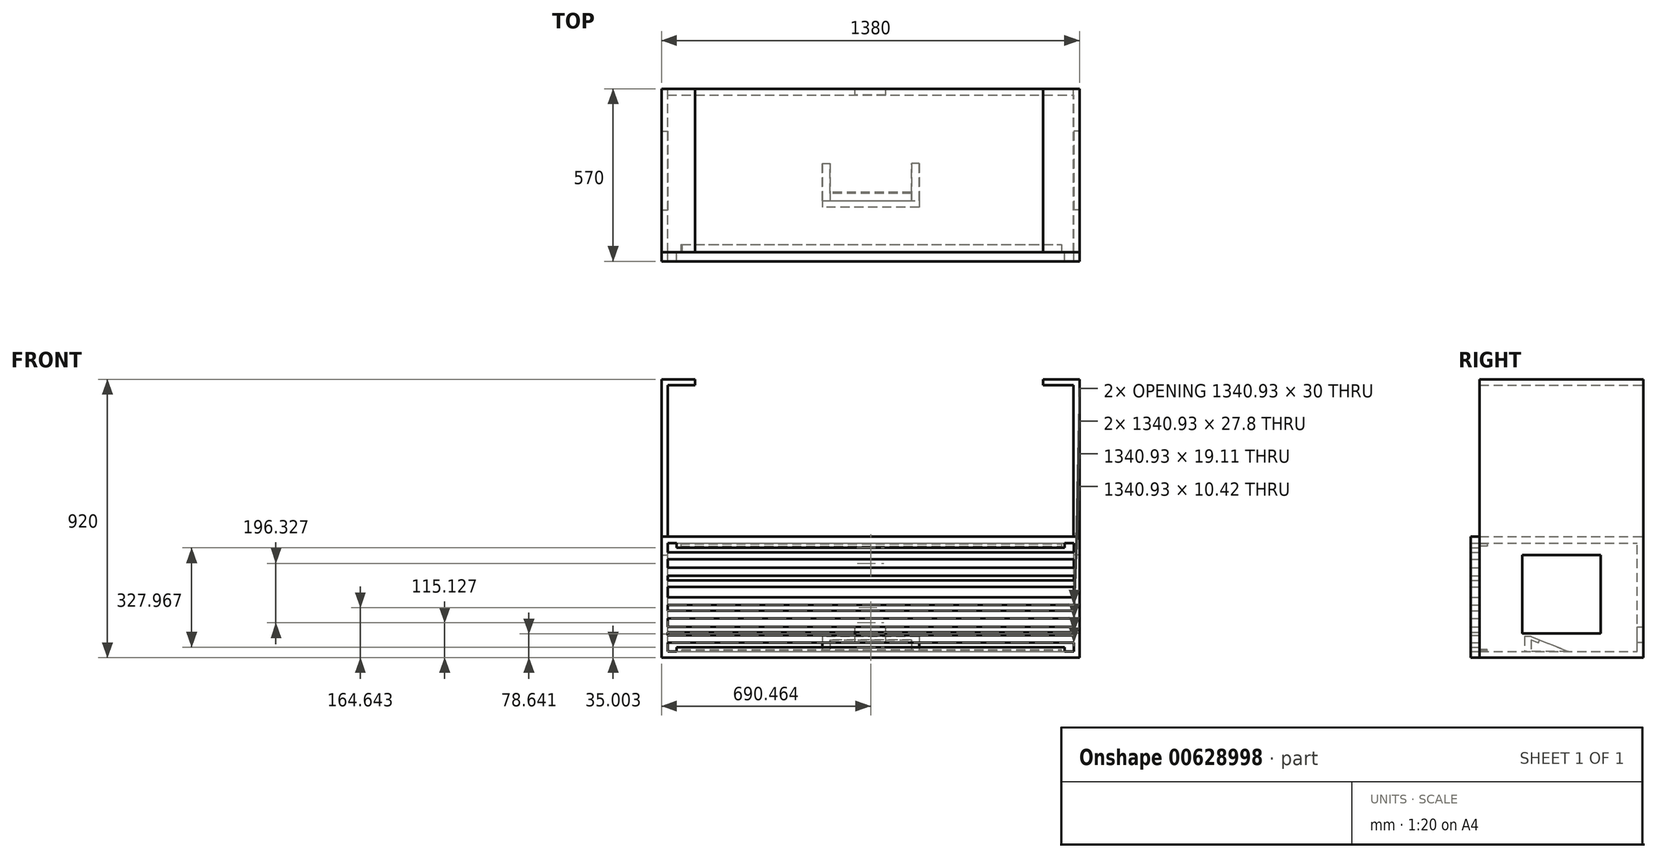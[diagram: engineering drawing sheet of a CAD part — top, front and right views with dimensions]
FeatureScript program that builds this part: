
annotation { "Feature Type Name" : "Feature", "Feature Type Description" : "" }
export const myFeature = defineFeature(function(context is Context, id is Id, definition is map)
    precondition{}
    {
        {
            var Q0;
            Q0=qCreatedBy(makeId("Front.planeOp"),FACE);
            var sketch = newSketch(context, id + "F0", { "sketchPlane" : qUnion([Q0])});
            skLineSegment(sketch, "E0", {"start": v(-401.13, 629.38) * mm, "end": v(-401.13, 129.38) * mm});
            skLineSegment(sketch, "E1", {"start": v(-401.13, -250.62) * mm, "end": v(938.87, -250.62) * mm});
            skLineSegment(sketch, "E2", {"start": v(-401.13, 629.38) * mm, "end": v(-361.13, 629.38) * mm});
            skLineSegment(sketch, "E3", {"start": v(938.87, 629.38) * mm, "end": v(838.87, 629.38) * mm});
            skLineSegment(sketch, "E4", {"start": v(-361.13, 629.38) * mm, "end": v(-361.13, 649.38) * mm});
            skLineSegment(sketch, "E5", {"start": v(-361.13, 649.38) * mm, "end": v(-421.13, 649.38) * mm});
            skLineSegment(sketch, "E6", {"start": v(-421.13, 649.38) * mm, "end": v(-421.13, -270.62) * mm});
            skLineSegment(sketch, "E7", {"start": v(-421.13, -270.62) * mm, "end": v(958.87, -270.62) * mm});
            skLineSegment(sketch, "E8", {"start": v(958.87, -270.62) * mm, "end": v(958.87, 649.38) * mm});
            skLineSegment(sketch, "E9", {"start": v(958.87, 649.38) * mm, "end": v(838.87, 649.38) * mm});
            skLineSegment(sketch, "E10", {"start": v(838.87, 649.38) * mm, "end": v(838.87, 629.38) * mm});
            skLineSegment(sketch, "E11", {"start": v(-401.13, 129.38) * mm, "end": v(938.87, 129.38) * mm});
            skLineSegment(sketch, "E12.trimOffspring", {"start": v(-401.13, 210.1) * mm, "end": v(-401.13, 129.38) * mm});
            skLineSegment(sketch, "E13.trimOffspring", {"start": v(938.87, 129.38) * mm, "end": v(938.87, 629.38) * mm});
            skLineSegment(sketch, "E14.trimOffspring", {"start": v(938.87, 129.38) * mm, "end": v(938.87, 210.1) * mm});
            skPoint(sketch, "E15.trimOffspring.start.orphan", {"position": v(-401.13, 0) * mm});
            skLineSegment(sketch, "E16.bottom", {"start": v(-401.13, -250.62) * mm, "end": v(939.8, -250.62) * mm});
            skLineSegment(sketch, "E16.top", {"start": v(-401.13, 107.35) * mm, "end": v(939.8, 107.35) * mm});
            skLineSegment(sketch, "E16.left", {"start": v(-401.13, -250.62) * mm, "end": v(-401.13, 107.35) * mm});
            skLineSegment(sketch, "E16.right", {"start": v(939.8, -250.62) * mm, "end": v(939.8, 107.35) * mm});
            skSolve(sketch);
        }
        {
            var Q0;
            Q0 = qSketchRegion(id + "F0", true);
            extrude(context, id + "F1", {"entities" : qUnion([Q0]), "depth" : 540 * mm, "offsetDistance" : 25 * mm});
        }
        {
            var Q0;
            Q0=makeQuery(id+"F1.opExtrude","SWEPT_FACE",FACE,{"disambiguationData":[OSD([sQuery(id+"F0.wireOp",EDGE,"E6")])]});
            var sketch = newSketch(context, id + "F2", { "sketchPlane" : qUnion([Q0])});
            skLineSegment(sketch, "E17", {"start": v(31.38, 116.22) * mm, "end": v(508.62, 116.22) * mm});
            skPoint(sketch, "E18.left.start.orphan", {"position": v(170.12, 0) * mm});
            skLineSegment(sketch, "E19.top", {"start": v(31.38, -239.23) * mm, "end": v(508.62, -239.23) * mm});
            skLineSegment(sketch, "E19.left", {"start": v(31.38, 116.22) * mm, "end": v(31.38, -239.23) * mm});
            skLineSegment(sketch, "E19.right", {"start": v(508.62, 116.22) * mm, "end": v(508.62, -239.23) * mm});
            skLineSegment(sketch, "E20", {"start": v(270, 116.22) * mm, "end": v(270, -239.23) * mm});
            skLineSegment(sketch, "E21", {"start": v(31.38, -61.5) * mm, "end": v(508.62, -61.5) * mm});
            skLineSegment(sketch, "E22.bottom", {"start": v(400, 68.5) * mm, "end": v(140, 68.5) * mm});
            skLineSegment(sketch, "E22.top", {"start": v(400, -191.5) * mm, "end": v(140, -191.5) * mm});
            skLineSegment(sketch, "E22.left", {"start": v(400, 68.5) * mm, "end": v(400, -191.5) * mm});
            skLineSegment(sketch, "E22.right", {"start": v(140, 68.5) * mm, "end": v(140, -191.5) * mm});
            skPoint(sketch, "E22.middle", {"position": v(270, -61.5) * mm});
            skSolve(sketch);
        }
        {
            var Q0;
            {var subQ0=sQuery(id+"F2.wireOp",EDGE,"E22.bottom");var subQ1=sQuery(id+"F2.wireOp",EDGE,"E20");var subQ2=makeQuery(id+"F2.imprint","INTERSECT",VERTEX,{"derivedFrom":[subQ1,subQ0]});Q0=makeQuery(id+"F2.imprint","IMPRINT",FACE,{"disambiguationData":[TD([[makeQuery(id+"F2.imprint","IMPRINT",EDGE,{"disambiguationData":[TD([[subQ2,-1.0]])],"derivedFrom":subQ1}),-1.0]])]});}
            var Q1;
            {var subQ0=sQuery(id+"F2.wireOp",EDGE,"E22.bottom");var subQ1=sQuery(id+"F2.wireOp",EDGE,"E20");var subQ2=makeQuery(id+"F2.imprint","INTERSECT",VERTEX,{"derivedFrom":[subQ1,subQ0]});Q1=makeQuery(id+"F2.imprint","IMPRINT",FACE,{"disambiguationData":[TD([[makeQuery(id+"F2.imprint","IMPRINT",EDGE,{"disambiguationData":[TD([[subQ2,-1.0]])],"derivedFrom":subQ1}),1.0]])]});}
            var Q2;
            {var subQ0=sQuery(id+"F2.wireOp",EDGE,"E21");var subQ1=sQuery(id+"F2.wireOp",EDGE,"E20");var subQ2=makeQuery(id+"F2.imprint","INTERSECT",VERTEX,{"derivedFrom":[subQ1,subQ0]});Q2=makeQuery(id+"F2.imprint","IMPRINT",FACE,{"disambiguationData":[TD([[makeQuery(id+"F2.imprint","IMPRINT",EDGE,{"disambiguationData":[TD([[subQ2,-1.0]])],"derivedFrom":subQ1}),1.0]])]});}
            var Q3;
            {var subQ0=sQuery(id+"F2.wireOp",EDGE,"E21");var subQ1=sQuery(id+"F2.wireOp",EDGE,"E20");var subQ2=makeQuery(id+"F2.imprint","INTERSECT",VERTEX,{"derivedFrom":[subQ1,subQ0]});Q3=makeQuery(id+"F2.imprint","IMPRINT",FACE,{"disambiguationData":[TD([[makeQuery(id+"F2.imprint","IMPRINT",EDGE,{"disambiguationData":[TD([[subQ2,-1.0]])],"derivedFrom":subQ1}),-1.0]])]});}
            extrude(context, id + "F3", {"entities" : qUnion([Q0, Q1, Q2, Q3]), "endBound" : BoundingType.SYMMETRIC, "depth" : 83 * mm, "offsetDistance" : 25 * mm});
        }
        {
            var Q0;
            Q0=makeQuery(id+"F3.opExtrude","SWEPT_BODY",BODY,{"disambiguationData":[OSD([sQuery(id+"F2.wireOp",EDGE,"E22.bottom"),sQuery(id+"F2.wireOp",EDGE,"E22.top"),sQuery(id+"F2.wireOp",EDGE,"E22.left"),sQuery(id+"F2.wireOp",EDGE,"E22.right")])]});
            var Q1;
            Q1=makeQuery(id+"F1.opExtrude","SWEPT_BODY",BODY,{"disambiguationData":[OSD([sQuery(id+"F0.wireOp",EDGE,"E0"),sQuery(id+"F0.wireOp",EDGE,"E1"),sQuery(id+"F0.wireOp",EDGE,"aRKKb0dd-PKcr-7rpU-zyVE-1iy4NY3TNUit"),sQuery(id+"F0.wireOp",EDGE,"E2"),sQuery(id+"F0.wireOp",EDGE,"E3"),sQuery(id+"F0.wireOp",EDGE,"E4"),sQuery(id+"F0.wireOp",EDGE,"E5"),sQuery(id+"F0.wireOp",EDGE,"E6"),sQuery(id+"F0.wireOp",EDGE,"E7"),sQuery(id+"F0.wireOp",EDGE,"E8"),sQuery(id+"F0.wireOp",EDGE,"E9"),sQuery(id+"F0.wireOp",EDGE,"E10")])]});
            booleanBodies(context, id + "F4", {"operationType" : BooleanOperationType.SUBTRACTION, "tools" : qUnion([Q0]), "targets" : qUnion([Q1])});
        }
        {
            var Q0;
            Q0=makeQuery(id+"F1.opExtrude","SWEPT_FACE",FACE,{"disambiguationData":[OSD([sQuery(id+"F0.wireOp",EDGE,"E8")])]});
            var sketch = newSketch(context, id + "F5", { "sketchPlane" : qUnion([Q0])});
            skLineSegment(sketch, "E23", {"start": v(-207.28, -229.23) * mm, "end": v(-207.28, -239.23) * mm});
            skLineSegment(sketch, "E24", {"start": v(-508.62, 107.17) * mm, "end": v(-31.38, 107.17) * mm});
            skLineSegment(sketch, "E25", {"start": v(-270, 107.17) * mm, "end": v(-270, -229.23) * mm});
            skLineSegment(sketch, "E26.bottom", {"start": v(-140, -191.03) * mm, "end": v(-400, -191.03) * mm});
            skLineSegment(sketch, "E26.top", {"start": v(-140, 68.97) * mm, "end": v(-400, 68.97) * mm});
            skLineSegment(sketch, "E26.left", {"start": v(-140, -191.03) * mm, "end": v(-140, 68.97) * mm});
            skLineSegment(sketch, "E26.right", {"start": v(-400, -191.03) * mm, "end": v(-400, 68.97) * mm});
            skPoint(sketch, "E26.middle", {"position": v(-270, -61.03) * mm});
            skSolve(sketch);
        }
        {
            var Q0;
            Q0 = qSketchRegion(id + "F5", true);
            var Q1;
            {var subQ1=sQuery(id+"F5.wireOp",EDGE,"LzoH4UWJ-LyBd-hfi7-cmpX-1RLCS41nivTr.bottom");Q1=makeQuery(id+"F5.imprint","IMPRINT",FACE,{"disambiguationData":[TD([[makeQuery(id+"F5.imprint","IMPRINT",EDGE,{"derivedFrom":subQ1}),-1.0]])]});}
            extrude(context, id + "F6", {"entities" : qUnion([Q0, Q1]), "endBound" : BoundingType.SYMMETRIC, "depth" : 500 * mm, "offsetDistance" : 25 * mm});
        }
        {
            var Q0;
            Q0=makeQuery(id+"F6.opExtrude","SWEPT_BODY",BODY,{"disambiguationData":[OSD([sQuery(id+"F5.wireOp",EDGE,"E26.bottom"),sQuery(id+"F5.wireOp",EDGE,"E26.top"),sQuery(id+"F5.wireOp",EDGE,"E26.left"),sQuery(id+"F5.wireOp",EDGE,"E26.right")])]});
            var Q1;
            Q1=makeQuery(id+"F1.opExtrude","SWEPT_BODY",BODY,{"disambiguationData":[OSD([sQuery(id+"F0.wireOp",EDGE,"E0"),sQuery(id+"F0.wireOp",EDGE,"E1"),sQuery(id+"F0.wireOp",EDGE,"aRKKb0dd-PKcr-7rpU-zyVE-1iy4NY3TNUit"),sQuery(id+"F0.wireOp",EDGE,"E2"),sQuery(id+"F0.wireOp",EDGE,"E3"),sQuery(id+"F0.wireOp",EDGE,"E4"),sQuery(id+"F0.wireOp",EDGE,"E5"),sQuery(id+"F0.wireOp",EDGE,"E6"),sQuery(id+"F0.wireOp",EDGE,"E7"),sQuery(id+"F0.wireOp",EDGE,"E8"),sQuery(id+"F0.wireOp",EDGE,"E9"),sQuery(id+"F0.wireOp",EDGE,"E10")])]});
            booleanBodies(context, id + "F7", {"operationType" : BooleanOperationType.SUBTRACTION, "tools" : qUnion([Q0]), "targets" : qUnion([Q1])});
        }
        {
            var Q0;
            Q0=makeQuery(id+"F1.opExtrude","SWEPT_FACE",FACE,{"disambiguationData":[OSD([sQuery(id+"F0.wireOp",EDGE,"E4")])]});
            extrude(context, id + "F8", {"entities" : qUnion([Q0]), "operationType" : NewBodyOperationType.ADD, "depth" : 50 * mm, "offsetDistance" : 25 * mm});
        }
        {
            var Q0;
            Q0=makeQuery(id+"FRXGy1kO0sc0PEi_1.opFillet","SPLIT",FACE,{"disambiguationData":[OD(3.0)],"derivedFrom":makeQuery(id+"F1.opExtrude","CAP_FACE",FACE,{"disambiguationData":[OSD([sQuery(id+"F0.wireOp",EDGE,"E0"),sQuery(id+"F0.wireOp",EDGE,"E2"),sQuery(id+"F0.wireOp",EDGE,"E3"),sQuery(id+"F0.wireOp",EDGE,"E4"),sQuery(id+"F0.wireOp",EDGE,"E5"),sQuery(id+"F0.wireOp",EDGE,"E6"),sQuery(id+"F0.wireOp",EDGE,"E7"),sQuery(id+"F0.wireOp",EDGE,"E8"),sQuery(id+"F0.wireOp",EDGE,"E9"),sQuery(id+"F0.wireOp",EDGE,"E10"),sQuery(id+"F0.wireOp",EDGE,"E11"),sQuery(id+"F0.wireOp",EDGE,"E12.trimOffspring"),sQuery(id+"F0.wireOp",EDGE,"E13.trimOffspring"),sQuery(id+"F0.wireOp",EDGE,"E14.trimOffspring"),sQuery(id+"F0.wireOp",EDGE,"E16.bottom"),sQuery(id+"F0.wireOp",EDGE,"E16.top"),sQuery(id+"F0.wireOp",EDGE,"E16.left"),sQuery(id+"F0.wireOp",EDGE,"E16.right")])],"isStart":false})});
            var sketch = newSketch(context, id + "F9", { "sketchPlane" : qUnion([Q0])});
            skLineSegment(sketch, "E27.bottom", {"start": v(-421.13, -270.62) * mm, "end": v(958.87, -270.62) * mm});
            skLineSegment(sketch, "E27.top", {"start": v(-421.13, 129.38) * mm, "end": v(958.87, 129.38) * mm});
            skLineSegment(sketch, "E27.left", {"start": v(-421.13, -270.62) * mm, "end": v(-421.13, 129.38) * mm});
            skLineSegment(sketch, "E27.right", {"start": v(958.87, -270.62) * mm, "end": v(958.87, 129.38) * mm});
            skLineSegment(sketch, "E28.bottom", {"start": v(-401.13, 107.35) * mm, "end": v(-371.13, 107.35) * mm});
            skLineSegment(sketch, "E28.top", {"start": v(-401.13, 77.35) * mm, "end": v(-371.13, 77.35) * mm});
            skLineSegment(sketch, "E28.left", {"start": v(-401.13, 107.35) * mm, "end": v(-401.13, 77.35) * mm});
            skLineSegment(sketch, "E28.right", {"start": v(-371.13, 107.35) * mm, "end": v(-371.13, 77.35) * mm});
            skLineSegment(sketch, "E29.bottom", {"start": v(-401.13, -250.62) * mm, "end": v(-371.13, -250.62) * mm});
            skLineSegment(sketch, "E29.top", {"start": v(-401.13, -220.62) * mm, "end": v(-371.13, -220.62) * mm});
            skLineSegment(sketch, "E29.left", {"start": v(-401.13, -250.62) * mm, "end": v(-401.13, -220.62) * mm});
            skLineSegment(sketch, "E29.right", {"start": v(-371.13, -250.62) * mm, "end": v(-371.13, -220.62) * mm});
            skLineSegment(sketch, "E30.bottom", {"start": v(939.8, 107.35) * mm, "end": v(909.8, 107.35) * mm});
            skLineSegment(sketch, "E30.top", {"start": v(939.8, 77.35) * mm, "end": v(909.8, 77.35) * mm});
            skLineSegment(sketch, "E30.left", {"start": v(939.8, 107.35) * mm, "end": v(939.8, 77.35) * mm});
            skLineSegment(sketch, "E30.right", {"start": v(909.8, 107.35) * mm, "end": v(909.8, 77.35) * mm});
            skLineSegment(sketch, "E31.bottom", {"start": v(939.8, -250.62) * mm, "end": v(909.8, -250.62) * mm});
            skLineSegment(sketch, "E31.top", {"start": v(939.8, -220.62) * mm, "end": v(909.8, -220.62) * mm});
            skLineSegment(sketch, "E31.left", {"start": v(939.8, -250.62) * mm, "end": v(939.8, -220.62) * mm});
            skLineSegment(sketch, "E31.right", {"start": v(909.8, -250.62) * mm, "end": v(909.8, -220.62) * mm});
            skLineSegment(sketch, "E32.bottom", {"start": v(-401.13, 54.73) * mm, "end": v(939.8, 54.73) * mm});
            skLineSegment(sketch, "E32.top", {"start": v(-401.13, 26.93) * mm, "end": v(939.8, 26.93) * mm});
            skLineSegment(sketch, "E32.left", {"start": v(-401.13, 54.73) * mm, "end": v(-401.13, 26.93) * mm});
            skLineSegment(sketch, "E32.right", {"start": v(939.8, 54.73) * mm, "end": v(939.8, 26.93) * mm});
            skLineSegment(sketch, "E33.bottom", {"start": v(-401.13, 0) * mm, "end": v(939.8, 0) * mm});
            skLineSegment(sketch, "E33.top", {"start": v(-401.13, -14.76) * mm, "end": v(939.8, -14.76) * mm});
            skLineSegment(sketch, "E33.left", {"start": v(-401.13, 0) * mm, "end": v(-401.13, -14.76) * mm});
            skLineSegment(sketch, "E33.right", {"start": v(939.8, 0) * mm, "end": v(939.8, -14.76) * mm});
            skLineSegment(sketch, "E34.bottom", {"start": v(939.8, -37.35) * mm, "end": v(-401.13, -37.35) * mm});
            skLineSegment(sketch, "E34.top", {"start": v(939.8, -71.63) * mm, "end": v(-401.13, -71.63) * mm});
            skLineSegment(sketch, "E34.left", {"start": v(939.8, -37.35) * mm, "end": v(939.8, -71.63) * mm});
            skLineSegment(sketch, "E34.right", {"start": v(-401.13, -37.35) * mm, "end": v(-401.13, -71.63) * mm});
            skLineSegment(sketch, "E35.bottom", {"start": v(-401.13, -96.42) * mm, "end": v(939.8, -96.42) * mm});
            skLineSegment(sketch, "E35.top", {"start": v(-401.13, -115.53) * mm, "end": v(939.8, -115.53) * mm});
            skLineSegment(sketch, "E35.left", {"start": v(-401.13, -96.42) * mm, "end": v(-401.13, -115.53) * mm});
            skLineSegment(sketch, "E35.right", {"start": v(939.8, -96.42) * mm, "end": v(939.8, -115.53) * mm});
            skLineSegment(sketch, "E36.bottom", {"start": v(939.8, -141.6) * mm, "end": v(-401.13, -141.6) * mm});
            skLineSegment(sketch, "E36.top", {"start": v(939.8, -169.4) * mm, "end": v(-401.13, -169.4) * mm});
            skLineSegment(sketch, "E36.left", {"start": v(939.8, -141.6) * mm, "end": v(939.8, -169.4) * mm});
            skLineSegment(sketch, "E36.right", {"start": v(-401.13, -141.6) * mm, "end": v(-401.13, -169.4) * mm});
            skLineSegment(sketch, "E37.bottom", {"start": v(-401.13, -197.2) * mm, "end": v(939.8, -197.2) * mm});
            skLineSegment(sketch, "E37.top", {"start": v(-401.13, -186.77) * mm, "end": v(939.8, -186.77) * mm});
            skLineSegment(sketch, "E37.left", {"start": v(-401.13, -197.2) * mm, "end": v(-401.13, -186.77) * mm});
            skLineSegment(sketch, "E37.right", {"start": v(939.8, -197.2) * mm, "end": v(939.8, -186.77) * mm});
            skLineSegment(sketch, "E38.bottom", {"start": v(-371.13, -220.62) * mm, "end": v(909.8, -220.62) * mm});
            skLineSegment(sketch, "E38.top", {"start": v(-371.13, -235.62) * mm, "end": v(909.8, -235.62) * mm});
            skLineSegment(sketch, "E38.left", {"start": v(-371.13, -220.62) * mm, "end": v(-371.13, -235.62) * mm});
            skLineSegment(sketch, "E38.right", {"start": v(909.8, -220.62) * mm, "end": v(909.8, -235.62) * mm});
            skLineSegment(sketch, "E39.bottom", {"start": v(-371.13, 77.35) * mm, "end": v(909.8, 77.35) * mm});
            skLineSegment(sketch, "E39.top", {"start": v(-371.13, 92.35) * mm, "end": v(909.8, 92.35) * mm});
            skLineSegment(sketch, "E39.left", {"start": v(-371.13, 77.35) * mm, "end": v(-371.13, 92.35) * mm});
            skLineSegment(sketch, "E39.right", {"start": v(909.8, 77.35) * mm, "end": v(909.8, 92.35) * mm});
            skLineSegment(sketch, "E40", {"start": v(-364.3, 92.35) * mm, "end": v(-364.3, 77.35) * mm});
            skSolve(sketch);
        }
        {
            var Q0;
            Q0=makeQuery(id+"F9.imprint","IMPRINT",FACE,{"disambiguationData":[TD([[makeQuery(id+"F9.imprint","IMPRINT",EDGE,{"derivedFrom":sQuery(id+"F9.wireOp",EDGE,"E27.bottom")}),1.0]])]});
            var sketch = newSketch(context, id + "F10", { "sketchPlane" : qUnion([Q0])});
            skLineSegment(sketch, "E41.bottom", {"start": v(-354.44, -248.81) * mm, "end": v(899.48, -248.81) * mm});
            skLineSegment(sketch, "E41.top", {"start": v(-354.44, -243.56) * mm, "end": v(899.48, -243.56) * mm});
            skLineSegment(sketch, "E41.left", {"start": v(-354.44, -248.81) * mm, "end": v(-354.44, -243.56) * mm});
            skLineSegment(sketch, "E41.right", {"start": v(899.48, -248.81) * mm, "end": v(899.48, -243.56) * mm});
            skLineSegment(sketch, "E42.bottom", {"start": v(-358.14, 105.24) * mm, "end": v(899.48, 105.24) * mm});
            skLineSegment(sketch, "E42.top", {"start": v(-358.14, 98.17) * mm, "end": v(899.48, 98.17) * mm});
            skLineSegment(sketch, "E42.left", {"start": v(-358.14, 105.24) * mm, "end": v(-358.14, 98.17) * mm});
            skLineSegment(sketch, "E42.right", {"start": v(899.48, 105.24) * mm, "end": v(899.48, 98.17) * mm});
            skSolve(sketch);
        }
        {
            var Q0;
            Q0 = qSketchRegion(id + "F9", true);
            extrude(context, id + "F11", {"entities" : qUnion([Q0]), "depth" : 30 * mm, "offsetDistance" : 25 * mm});
        }
        {
            var Q0;
            Q0 = qSketchRegion(id + "F10", true);
            extrude(context, id + "F12", {"entities" : qUnion([Q0]), "operationType" : NewBodyOperationType.ADD, "depth" : -25 * mm, "offsetDistance" : 25 * mm});
        }
        {
            var Q0;
            {var subQ0=sQuery(id+"F0.wireOp",EDGE,"E4");Q0=makeQuery(id+"F8.boolean.opBoolean","MERGE",FACE,{"derivedFrom":[makeQuery(id+"F1.opExtrude","CAP_FACE",FACE,{"disambiguationData":[OSD([sQuery(id+"F0.wireOp",EDGE,"E0"),sQuery(id+"F0.wireOp",EDGE,"E2"),sQuery(id+"F0.wireOp",EDGE,"E3"),subQ0,sQuery(id+"F0.wireOp",EDGE,"E5"),sQuery(id+"F0.wireOp",EDGE,"E6"),sQuery(id+"F0.wireOp",EDGE,"E7"),sQuery(id+"F0.wireOp",EDGE,"E8"),sQuery(id+"F0.wireOp",EDGE,"E9"),sQuery(id+"F0.wireOp",EDGE,"E10"),sQuery(id+"F0.wireOp",EDGE,"E11"),sQuery(id+"F0.wireOp",EDGE,"E12.trimOffspring"),sQuery(id+"F0.wireOp",EDGE,"E13.trimOffspring"),sQuery(id+"F0.wireOp",EDGE,"E14.trimOffspring"),sQuery(id+"F0.wireOp",EDGE,"E16.bottom"),sQuery(id+"F0.wireOp",EDGE,"E16.top"),sQuery(id+"F0.wireOp",EDGE,"E16.left"),sQuery(id+"F0.wireOp",EDGE,"E16.right")])],"isStart":true}),makeQuery(id+"F8.opExtrude","SWEPT_FACE",FACE,{"disambiguationData":[OSD([subQ0]),TDD([makeQuery(id+"F1.opExtrude","CAP_EDGE",EDGE,{"disambiguationData":[OSD([subQ0])],"isStart":true})])]})]});}
            var sketch = newSketch(context, id + "F13", { "sketchPlane" : qUnion([Q0])});
            skLineSegment(sketch, "E43.bottom", {"start": v(-939.8, 107.35) * mm, "end": v(401.13, 107.35) * mm});
            skLineSegment(sketch, "E43.top", {"start": v(-939.8, -250.62) * mm, "end": v(401.13, -250.62) * mm});
            skLineSegment(sketch, "E43.left", {"start": v(-939.8, 107.35) * mm, "end": v(-939.8, -250.62) * mm});
            skLineSegment(sketch, "E43.right", {"start": v(401.13, 107.35) * mm, "end": v(401.13, -250.62) * mm});
            skSolve(sketch);
        }
        {
            var Q0;
            Q0 = qSketchRegion(id + "F13", true);
            extrude(context, id + "F14", {"entities" : qUnion([Q0]), "operationType" : NewBodyOperationType.ADD, "depth" : -20 * mm, "offsetDistance" : 25 * mm});
        }
        {
            var Q0;
            Q0=makeQuery(id+"F1.opExtrude","SWEPT_FACE",FACE,{"disambiguationData":[OSD([sQuery(id+"F0.wireOp",EDGE,"E16.bottom")])]});
            var sketch = newSketch(context, id + "F15", { "sketchPlane" : qUnion([Q0])});
            skLineSegment(sketch, "E44", {"start": v(269.33, -20) * mm, "end": v(269.33, -370) * mm});
            skLineSegment(sketch, "E45.bottom", {"start": v(269.33, -370) * mm, "end": v(134.33, -370) * mm});
            skLineSegment(sketch, "E45.top", {"start": v(210.37, -391.62) * mm, "end": v(134.33, -391.62) * mm});
            skLineSegment(sketch, "E45.right", {"start": v(134.33, -370) * mm, "end": v(134.33, -391.62) * mm});
            skLineSegment(sketch, "E46.bottom", {"start": v(269.33, -370) * mm, "end": v(404.33, -370) * mm});
            skLineSegment(sketch, "E46.top", {"start": v(269.33, -391.62) * mm, "end": v(404.33, -391.62) * mm});
            skLineSegment(sketch, "E46.right", {"start": v(404.33, -370) * mm, "end": v(404.33, -391.62) * mm});
            skLineSegment(sketch, "E47.trimOffspring", {"start": v(269.33, -391.62) * mm, "end": v(269.33, -540) * mm});
            skLineSegment(sketch, "E48", {"start": v(210.37, -391.62) * mm, "end": v(269.33, -391.62) * mm});
            skSolve(sketch);
        }
        {
            var Q0;
            Q0 = qSketchRegion(id + "F15", true);
            extrude(context, id + "F16", {"entities" : qUnion([Q0]), "operationType" : NewBodyOperationType.ADD, "depth" : 50 * mm, "offsetDistance" : 25 * mm});
        }
        {
            var Q0;
            Q0=makeQuery(id+"F16.opExtrude","SWEPT_FACE",FACE,{"disambiguationData":[OSD([sQuery(id+"F15.wireOp",EDGE,"E46.right")])]});
            var sketch = newSketch(context, id + "F17", { "sketchPlane" : qUnion([Q0])});
            skLineSegment(sketch, "E49", {"start": v(-391.62, -250.62) * mm, "end": v(-391.62, -200.62) * mm});
            skLineSegment(sketch, "E50", {"start": v(-391.62, -200.62) * mm, "end": v(-370, -200.62) * mm});
            skLineSegment(sketch, "E51", {"start": v(-370, -200.62) * mm, "end": v(-246.62, -250.62) * mm});
            skLineSegment(sketch, "E52", {"start": v(-246.62, -250.62) * mm, "end": v(-391.62, -250.62) * mm});
            skSolve(sketch);
        }
        {
            var Q0;
            Q0 = qSketchRegion(id + "F17", true);
            extrude(context, id + "F18", {"entities" : qUnion([Q0]), "operationType" : NewBodyOperationType.ADD, "depth" : 25 * mm, "offsetDistance" : 25 * mm});
        }
        {
            var Q0;
            Q0=makeQuery(id+"F16.opExtrude","SWEPT_FACE",FACE,{"disambiguationData":[OSD([sQuery(id+"F15.wireOp",EDGE,"E45.right")])]});
            var sketch = newSketch(context, id + "F19", { "sketchPlane" : qUnion([Q0])});
            skLineSegment(sketch, "E53", {"start": v(391.62, -250.62) * mm, "end": v(391.62, -200.62) * mm});
            skLineSegment(sketch, "E54", {"start": v(391.62, -200.62) * mm, "end": v(370, -200.62) * mm});
            skLineSegment(sketch, "E55", {"start": v(370, -200.62) * mm, "end": v(246.62, -250.62) * mm});
            skLineSegment(sketch, "E56", {"start": v(246.62, -250.62) * mm, "end": v(391.62, -250.62) * mm});
            skSolve(sketch);
        }
        {
            var Q0;
            Q0 = qSketchRegion(id + "F19", true);
            extrude(context, id + "F20", {"entities" : qUnion([Q0]), "operationType" : NewBodyOperationType.ADD, "depth" : 25 * mm, "offsetDistance" : 25 * mm});
        }
        {
            var Q0;
            Q0=makeQuery(id+"F18.opExtrude","SWEPT_FACE",FACE,{"disambiguationData":[OSD([sQuery(id+"F17.wireOp",EDGE,"E51")])]});
            var sketch = newSketch(context, id + "F21", { "sketchPlane" : qUnion([Q0])});
            skLineSegment(sketch, "E57", {"start": v(404.33, -237.56) * mm, "end": v(134.33, -237.56) * mm});
            skLineSegment(sketch, "E58", {"start": v(404.33, -267.56) * mm, "end": v(404.33, -237.56) * mm});
            skLineSegment(sketch, "E59", {"start": v(134.33, -267.56) * mm, "end": v(404.33, -267.56) * mm});
            skLineSegment(sketch, "E60", {"start": v(134.33, -237.56) * mm, "end": v(134.33, -267.56) * mm});
            skSolve(sketch);
        }
        {
            var Q0;
            Q0 = qSketchRegion(id + "F21", true);
            extrude(context, id + "F22", {"entities" : qUnion([Q0]), "operationType" : NewBodyOperationType.ADD, "oppositeDirection" : true, "depth" : 11 * mm, "offsetDistance" : 25 * mm});
        }
        {
            var Q0;
            {var subQ0=sQuery(id+"F0.wireOp",EDGE,"E4");Q0=makeQuery(id+"F14.boolean.opBoolean","MERGE",FACE,{"derivedFrom":[makeQuery(id+"F8.boolean.opBoolean","MERGE",FACE,{"derivedFrom":[makeQuery(id+"F1.opExtrude","CAP_FACE",FACE,{"disambiguationData":[OSD([sQuery(id+"F0.wireOp",EDGE,"E0"),sQuery(id+"F0.wireOp",EDGE,"E2"),sQuery(id+"F0.wireOp",EDGE,"E3"),subQ0,sQuery(id+"F0.wireOp",EDGE,"E5"),sQuery(id+"F0.wireOp",EDGE,"E6"),sQuery(id+"F0.wireOp",EDGE,"E7"),sQuery(id+"F0.wireOp",EDGE,"E8"),sQuery(id+"F0.wireOp",EDGE,"E9"),sQuery(id+"F0.wireOp",EDGE,"E10"),sQuery(id+"F0.wireOp",EDGE,"E11"),sQuery(id+"F0.wireOp",EDGE,"E12.trimOffspring"),sQuery(id+"F0.wireOp",EDGE,"E13.trimOffspring"),sQuery(id+"F0.wireOp",EDGE,"E14.trimOffspring"),sQuery(id+"F0.wireOp",EDGE,"E16.bottom"),sQuery(id+"F0.wireOp",EDGE,"E16.top"),sQuery(id+"F0.wireOp",EDGE,"E16.left"),sQuery(id+"F0.wireOp",EDGE,"E16.right")])],"isStart":true}),makeQuery(id+"F8.opExtrude","SWEPT_FACE",FACE,{"disambiguationData":[OSD([subQ0]),TDD([makeQuery(id+"F1.opExtrude","CAP_EDGE",EDGE,{"disambiguationData":[OSD([subQ0])],"isStart":true})])]})]}),makeQuery(id+"F14.opExtrude","CAP_FACE",FACE,{"disambiguationData":[OSD([sQuery(id+"F13.wireOp",EDGE,"E43.bottom"),sQuery(id+"F13.wireOp",EDGE,"E43.top"),sQuery(id+"F13.wireOp",EDGE,"E43.left"),sQuery(id+"F13.wireOp",EDGE,"E43.right")])],"isStart":true})]});}
            var sketch = newSketch(context, id + "F23", { "sketchPlane" : qUnion([Q0])});
            skLineSegment(sketch, "E61", {"start": v(-268.87, 129.38) * mm, "end": v(-268.87, -270.62) * mm});
            skLineSegment(sketch, "E62", {"start": v(-268.87, -270.62) * mm, "end": v(-268.87, -219.78) * mm});
            skLineSegment(sketch, "E63", {"start": v(-268.87, -219.78) * mm, "end": v(-218.87, -219.78) * mm});
            skLineSegment(sketch, "E64", {"start": v(-268.87, -219.78) * mm, "end": v(-318.87, -219.78) * mm});
            skLineSegment(sketch, "E65.bottom", {"start": v(-218.87, -219.78) * mm, "end": v(-318.87, -219.78) * mm});
            skLineSegment(sketch, "E65.top", {"start": v(-218.87, -219.78) * mm, "end": v(-318.87, -219.78) * mm});
            skLineSegment(sketch, "E65.left", {"start": v(-218.87, -219.78) * mm, "end": v(-218.87, -219.78) * mm});
            skLineSegment(sketch, "E65.right", {"start": v(-318.87, -219.78) * mm, "end": v(-318.87, -219.78) * mm});
            skLineSegment(sketch, "E66.bottom", {"start": v(-318.87, -219.78) * mm, "end": v(-217.61, -219.78) * mm});
            skLineSegment(sketch, "E66.top", {"start": v(-318.87, -169.4) * mm, "end": v(-217.61, -169.4) * mm});
            skLineSegment(sketch, "E66.left", {"start": v(-318.87, -219.78) * mm, "end": v(-318.87, -169.4) * mm});
            skLineSegment(sketch, "E66.right", {"start": v(-217.61, -219.78) * mm, "end": v(-217.61, -169.4) * mm});
            skSolve(sketch);
        }
        {
            var Q0;
            {var subQ0=sQuery(id+"F23.wireOp",EDGE,"E66.right");Q0=makeQuery(id+"F23.imprint","IMPRINT",FACE,{"disambiguationData":[TD([[makeQuery(id+"F23.imprint","IMPRINT",EDGE,{"derivedFrom":subQ0}),1.0]])]});}
            var Q1;
            {var subQ5=sQuery(id+"F23.wireOp",EDGE,"E66.left");Q1=makeQuery(id+"F23.imprint","IMPRINT",FACE,{"disambiguationData":[TD([[makeQuery(id+"F23.imprint","IMPRINT",EDGE,{"derivedFrom":subQ5}),-1.0]])]});}
            extrude(context, id + "F24", {"entities" : qUnion([Q0, Q1]), "depth" : -60 * mm, "offsetDistance" : 25 * mm});
        }
        {
            var Q0;
            Q0=makeQuery(id+"F24.opExtrude","SWEPT_BODY",BODY,{"disambiguationData":[OSD([sQuery(id+"F23.wireOp",EDGE,"E66.bottom"),sQuery(id+"F23.wireOp",EDGE,"E66.top"),sQuery(id+"F23.wireOp",EDGE,"E66.left"),sQuery(id+"F23.wireOp",EDGE,"E66.right")])]});
            var Q1;
            Q1=makeQuery(id+"F1.opExtrude","SWEPT_BODY",BODY,{"disambiguationData":[OSD([sQuery(id+"F0.wireOp",EDGE,"E0"),sQuery(id+"F0.wireOp",EDGE,"E2"),sQuery(id+"F0.wireOp",EDGE,"E3"),sQuery(id+"F0.wireOp",EDGE,"E4"),sQuery(id+"F0.wireOp",EDGE,"E5"),sQuery(id+"F0.wireOp",EDGE,"E6"),sQuery(id+"F0.wireOp",EDGE,"E7"),sQuery(id+"F0.wireOp",EDGE,"E8"),sQuery(id+"F0.wireOp",EDGE,"E9"),sQuery(id+"F0.wireOp",EDGE,"E10"),sQuery(id+"F0.wireOp",EDGE,"E11"),sQuery(id+"F0.wireOp",EDGE,"E12.trimOffspring"),sQuery(id+"F0.wireOp",EDGE,"E13.trimOffspring"),sQuery(id+"F0.wireOp",EDGE,"E14.trimOffspring"),sQuery(id+"F0.wireOp",EDGE,"E16.bottom"),sQuery(id+"F0.wireOp",EDGE,"E16.top"),sQuery(id+"F0.wireOp",EDGE,"E16.left"),sQuery(id+"F0.wireOp",EDGE,"E16.right")])]});
            booleanBodies(context, id + "F25", {"operationType" : BooleanOperationType.SUBTRACTION, "tools" : qUnion([Q0]), "targets" : qUnion([Q1])});
        }
    });
